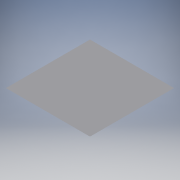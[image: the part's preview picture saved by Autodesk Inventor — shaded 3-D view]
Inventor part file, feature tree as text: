
AUTODESK INVENTOR PART (.ipt)
format: ipt  version: 2018 (Build 220112000, 112)  size: 95,744 bytes
history: native  units: mm
features: extrude x1, chamfer x1, sketch x1
ambient origin geometry x8: Origin, YZ Plane, XZ Plane, XY Plane, X Axis, Y Axis, Z Axis, Center Point
bodies: Volumenkörper1 (feature_tree)
feature tree (3):
  extrude  "Extrusion1"  Depth=20.0mm
  chamfer  "Fase1"  Distance=20.0mm
  sketch  "Skizze1"  dims[d0=500.0mm d1=450.0mm d2=20.0mm d3=0.0mm d4=20.0mm d5=2.0mm d6=45.0deg]
